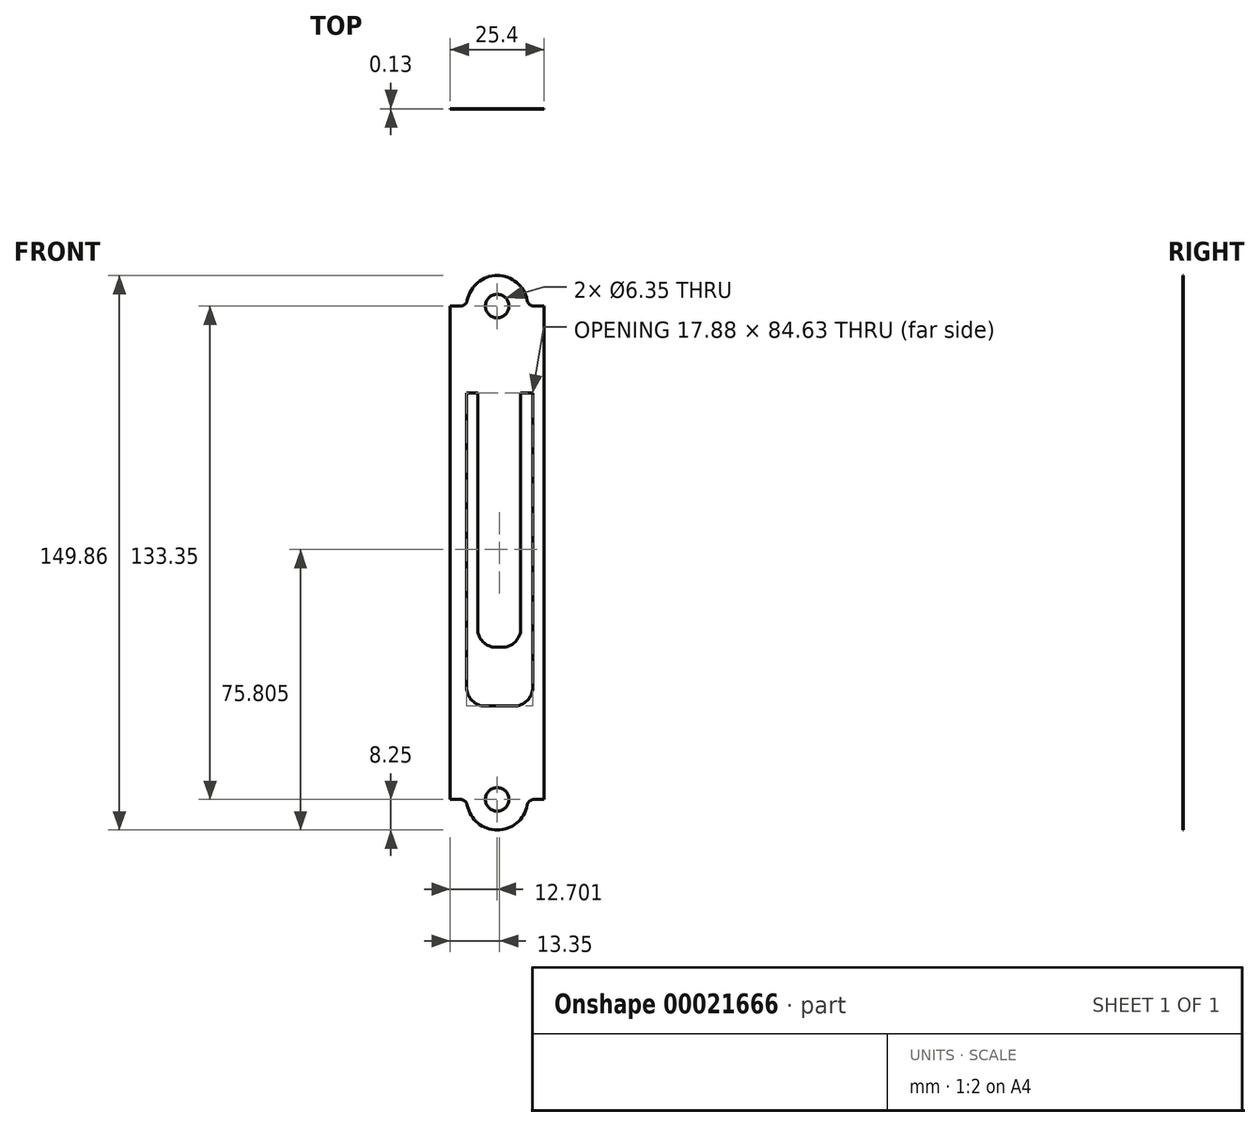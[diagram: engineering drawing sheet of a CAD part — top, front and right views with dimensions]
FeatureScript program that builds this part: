
annotation { "Feature Type Name" : "Feature", "Feature Type Description" : "" }
export const myFeature = defineFeature(function(context is Context, id is Id, definition is map)
    precondition{}
    {
        {
            var Q0;
            Q0=qCreatedBy(makeId("Front.planeOp"),FACE);
            var sketch = newSketch(context, id + "F0", { "sketchPlane" : qUnion([Q0])});
            skLineSegment(sketch, "E0.bottom", {"start": v(-22.29, 61.12) * mm, "end": v(-19.57, 61.12) * mm});
            skLineSegment(sketch, "E0.top", {"start": v(-22.29, -72.23) * mm, "end": v(-19.57, -72.23) * mm});
            skLineSegment(sketch, "E0.left", {"start": v(-22.29, 61.12) * mm, "end": v(-22.29, -72.23) * mm});
            skLineSegment(sketch, "E0.right", {"start": v(3.11, 61.12) * mm, "end": v(3.11, -72.23) * mm});
            skArc(sketch, "E1", {"start": v(-1.48, 62.67) * mm, "mid": v(-9.59, 69.38) * mm, "end": v(-17.7, 62.67) * mm});
            skArc(sketch, "E2", {"start": v(-17.7, -73.78) * mm, "mid": v(-9.59, -80.48) * mm, "end": v(-1.48, -73.78) * mm});
            skLineSegment(sketch, "E3.trimOffspring", {"start": v(0.4, 61.12) * mm, "end": v(3.11, 61.12) * mm});
            skLineSegment(sketch, "E4.trimOffspring", {"start": v(0.4, -72.23) * mm, "end": v(3.11, -72.23) * mm});
            skPoint(sketch, "E5.visualSharp", {"position": v(-17.84, 61.12) * mm});
            skArc(sketch, "E5.filletArc", {"start": v(-19.57, 61.12) * mm, "mid": v(-18.35, 61.56) * mm, "end": v(-17.7, 62.67) * mm});
            skPoint(sketch, "E6.visualSharp", {"position": v(-1.33, 61.12) * mm});
            skArc(sketch, "E6.filletArc", {"start": v(-1.48, 62.67) * mm, "mid": v(-0.82, 61.56) * mm, "end": v(0.4, 61.12) * mm});
            skPoint(sketch, "E7.visualSharp", {"position": v(-17.84, -72.23) * mm});
            skArc(sketch, "E7.filletArc", {"start": v(-17.7, -73.78) * mm, "mid": v(-18.35, -72.67) * mm, "end": v(-19.57, -72.23) * mm});
            skPoint(sketch, "E8.visualSharp", {"position": v(-1.33, -72.23) * mm});
            skArc(sketch, "E8.filletArc", {"start": v(0.4, -72.23) * mm, "mid": v(-0.82, -72.67) * mm, "end": v(-1.48, -73.78) * mm});
            skCircle(sketch, "E9", {"center": v(-9.59, 61.12) * mm, "radius": 3.18 * mm});
            skCircle(sketch, "E10", {"center": v(-9.59, -72.23) * mm, "radius": 3.18 * mm});
            skLineSegment(sketch, "E11.top", {"start": v(-9.82, -31.12) * mm, "end": v(-8.32, -31.12) * mm});
            skLineSegment(sketch, "E11.left", {"start": v(-14.9, 37.64) * mm, "end": v(-14.9, -26.04) * mm});
            skLineSegment(sketch, "E11.right", {"start": v(-3.24, 37.64) * mm, "end": v(-3.24, -26.04) * mm});
            skLineSegment(sketch, "E12.bottom", {"start": v(-17.88, 37.64) * mm, "end": v(-14.9, 37.64) * mm});
            skLineSegment(sketch, "E12.top", {"start": v(-12.8, -46.99) * mm, "end": v(-5.08, -46.99) * mm});
            skLineSegment(sketch, "E12.left", {"start": v(-17.88, 37.64) * mm, "end": v(-17.88, -41.9) * mm});
            skLineSegment(sketch, "E12.right", {"start": v(0, 37.64) * mm, "end": v(0, -41.9) * mm});
            skLineSegment(sketch, "E13.trimOffspring", {"start": v(-3.24, 37.64) * mm, "end": v(0, 37.64) * mm});
            skPoint(sketch, "E14.visualSharp", {"position": v(-14.9, -31.12) * mm});
            skArc(sketch, "E14.filletArc", {"start": v(-14.9, -26.04) * mm, "mid": v(-13.41, -29.63) * mm, "end": v(-9.82, -31.12) * mm});
            skPoint(sketch, "E15.visualSharp", {"position": v(-3.24, -31.12) * mm});
            skArc(sketch, "E15.filletArc", {"start": v(-8.32, -31.12) * mm, "mid": v(-4.73, -29.63) * mm, "end": v(-3.24, -26.04) * mm});
            skPoint(sketch, "E16.visualSharp", {"position": v(-17.88, -46.99) * mm});
            skArc(sketch, "E16.filletArc", {"start": v(-17.88, -41.9) * mm, "mid": v(-16.4, -45.5) * mm, "end": v(-12.8, -46.99) * mm});
            skPoint(sketch, "E17.visualSharp", {"position": v(0, -46.99) * mm});
            skArc(sketch, "E17.filletArc", {"start": v(-5.08, -46.99) * mm, "mid": v(-1.49, -45.5) * mm, "end": v(0, -41.9) * mm});
            skSolve(sketch);
        }
        {
            var Q0;
            Q0=makeQuery(id+"F0.imprint","IMPRINT",FACE,{"disambiguationData":[TD([[makeQuery(id+"F0.imprint","IMPRINT",EDGE,{"derivedFrom":sQuery(id+"F0.wireOp",EDGE,"E0.bottom")}),-1.0]])]});
            extrude(context, id + "F1", {"entities" : qUnion([Q0]), "depth" : 0.13 * mm});
        }
    });
